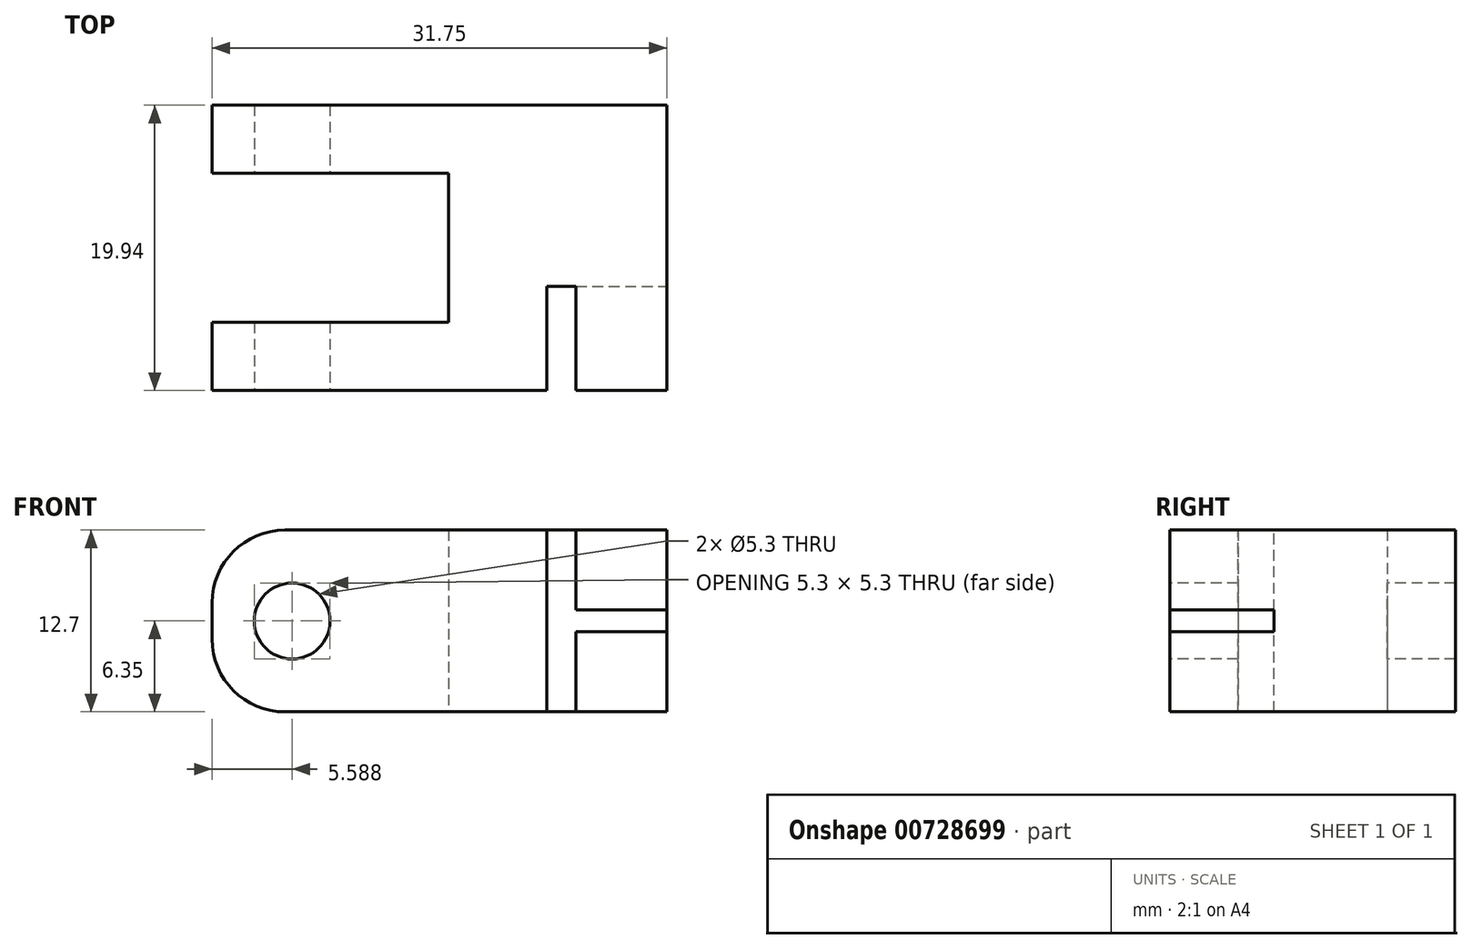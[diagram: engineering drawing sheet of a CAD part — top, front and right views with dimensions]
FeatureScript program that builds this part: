
annotation { "Feature Type Name" : "Feature", "Feature Type Description" : "" }
export const myFeature = defineFeature(function(context is Context, id is Id, definition is map)
    precondition{}
    {
        {
            var Q0;
            Q0=qCreatedBy(makeId("Top.planeOp"),FACE);
            var sketch = newSketch(context, id + "F0", { "sketchPlane" : qUnion([Q0])});
            skLineSegment(sketch, "E0", {"start": v(0, 0) * mm, "end": v(0, -4.76) * mm});
            skLineSegment(sketch, "E1", {"start": v(0, -4.76) * mm, "end": v(25.4, -4.76) * mm});
            skLineSegment(sketch, "E2", {"start": v(0, 0) * mm, "end": v(16.51, 0) * mm});
            skLineSegment(sketch, "E3", {"start": v(16.51, 0) * mm, "end": v(16.51, 10.41) * mm});
            skLineSegment(sketch, "E4", {"start": v(16.51, 10.41) * mm, "end": v(0, 10.41) * mm});
            skLineSegment(sketch, "E5", {"start": v(0, 10.41) * mm, "end": v(0, 15.18) * mm});
            skLineSegment(sketch, "E6", {"start": v(0, 15.18) * mm, "end": v(31.75, 15.18) * mm});
            skLineSegment(sketch, "E7", {"start": v(25.4, -4.76) * mm, "end": v(31.75, -4.76) * mm});
            skLineSegment(sketch, "E8", {"start": v(31.75, -4.76) * mm, "end": v(31.75, 15.18) * mm});
            skSolve(sketch);
        }
        {
            var Q0;
            Q0=qSketchRegion(id+"F0",true);
            extrude(context, id + "F1", {"entities" : qUnion([Q0]), "depth" : 12.7 * mm, "offsetDistance" : 25.4 * mm});
        }
        {
            var Q0;
            Q0=makeQuery(id+"F1.opExtrude","SWEPT_FACE",FACE,{"disambiguationData":[OSD([sQuery(id+"F0.wireOp",EDGE,"E1"),sQuery(id+"F0.wireOp",EDGE,"E7")])]});
            var sketch = newSketch(context, id + "F2", { "sketchPlane" : qUnion([Q0])});
            skCircle(sketch, "E9", {"center": v(5.59, 6.35) * mm, "radius": 2.65 * mm});
            skSolve(sketch);
        }
        {
            var Q0;
            Q0=qSketchRegion(id+"F2",true);
            extrude(context, id + "F3", {"entities" : qUnion([Q0]), "operationType" : NewBodyOperationType.REMOVE, "oppositeDirection" : true, "depth" : 51.82 * mm, "offsetDistance" : 25.4 * mm});
        }
        {
            var Q0;
            Q0=makeQuery(id+"F1.opExtrude","CAP_EDGE",EDGE,{"disambiguationData":[OSD([sQuery(id+"F0.wireOp",EDGE,"E0")])],"isStart":false});
            var Q1;
            Q1=makeQuery(id+"F1.opExtrude","CAP_EDGE",EDGE,{"disambiguationData":[OSD([sQuery(id+"F0.wireOp",EDGE,"E5")])],"isStart":false});
            var Q2;
            Q2=makeQuery(id+"F1.opExtrude","CAP_EDGE",EDGE,{"disambiguationData":[OSD([sQuery(id+"F0.wireOp",EDGE,"E0")])],"isStart":true});
            var Q3;
            Q3=makeQuery(id+"F1.opExtrude","CAP_EDGE",EDGE,{"disambiguationData":[OSD([sQuery(id+"F0.wireOp",EDGE,"E5")])],"isStart":true});
            fillet(context, id + "F4", {"entities" : qUnion([Q0, Q1, Q2, Q3]), "radius" : 5.08 * mm, "tangentPropagation" : true, "allowEdgeOverflow" : false});
        }
        {
            var Q0;
            Q0=makeQuery(id+"F1.opExtrude","SWEPT_FACE",FACE,{"disambiguationData":[OSD([sQuery(id+"F0.wireOp",EDGE,"E1"),sQuery(id+"F0.wireOp",EDGE,"E7")])]});
            var sketch = newSketch(context, id + "F5", { "sketchPlane" : qUnion([Q0])});
            skLineSegment(sketch, "E10", {"start": v(25.4, 14.79) * mm, "end": v(25.4, -2.13) * mm});
            skLineSegment(sketch, "E11", {"start": v(25.4, -2.13) * mm, "end": v(23.37, -2.13) * mm});
            skLineSegment(sketch, "E12", {"start": v(23.37, -2.13) * mm, "end": v(23.37, 14.79) * mm});
            skLineSegment(sketch, "E13", {"start": v(23.37, 14.79) * mm, "end": v(25.4, 14.79) * mm});
            skPoint(sketch, "E14.end.orphan", {"position": v(34.38, -2.13) * mm});
            skPoint(sketch, "E15.start.orphan", {"position": v(31.75, 6.35) * mm});
            skLineSegment(sketch, "E16", {"start": v(31.75, 6.35) * mm, "end": v(13.69, 6.35) * mm, "construction": true});
            skLineSegment(sketch, "E17", {"start": v(25.4, 5.59) * mm, "end": v(31.75, 5.59) * mm});
            skLineSegment(sketch, "E18.MirrorCS", {"start": v(25.4, 7.11) * mm, "end": v(31.75, 7.11) * mm});
            skSolve(sketch);
        }
        {
            var Q0;
            Q0=qSketchRegion(id+"F5",true);
            var Q1;
            {var subQ0=sQuery(id+"F5.wireOp",EDGE,"E17");Q1=makeQuery(id+"F5.imprint","IMPRINT",FACE,{"disambiguationData":[TD([[makeQuery(id+"F5.imprint","IMPRINT",EDGE,{"derivedFrom":subQ0}),1.0]])]});}
            extrude(context, id + "F6", {"entities" : qUnion([Q0, Q1]), "operationType" : NewBodyOperationType.REMOVE, "oppositeDirection" : true, "depth" : 7.3 * mm, "offsetDistance" : 25.4 * mm});
        }
    });
